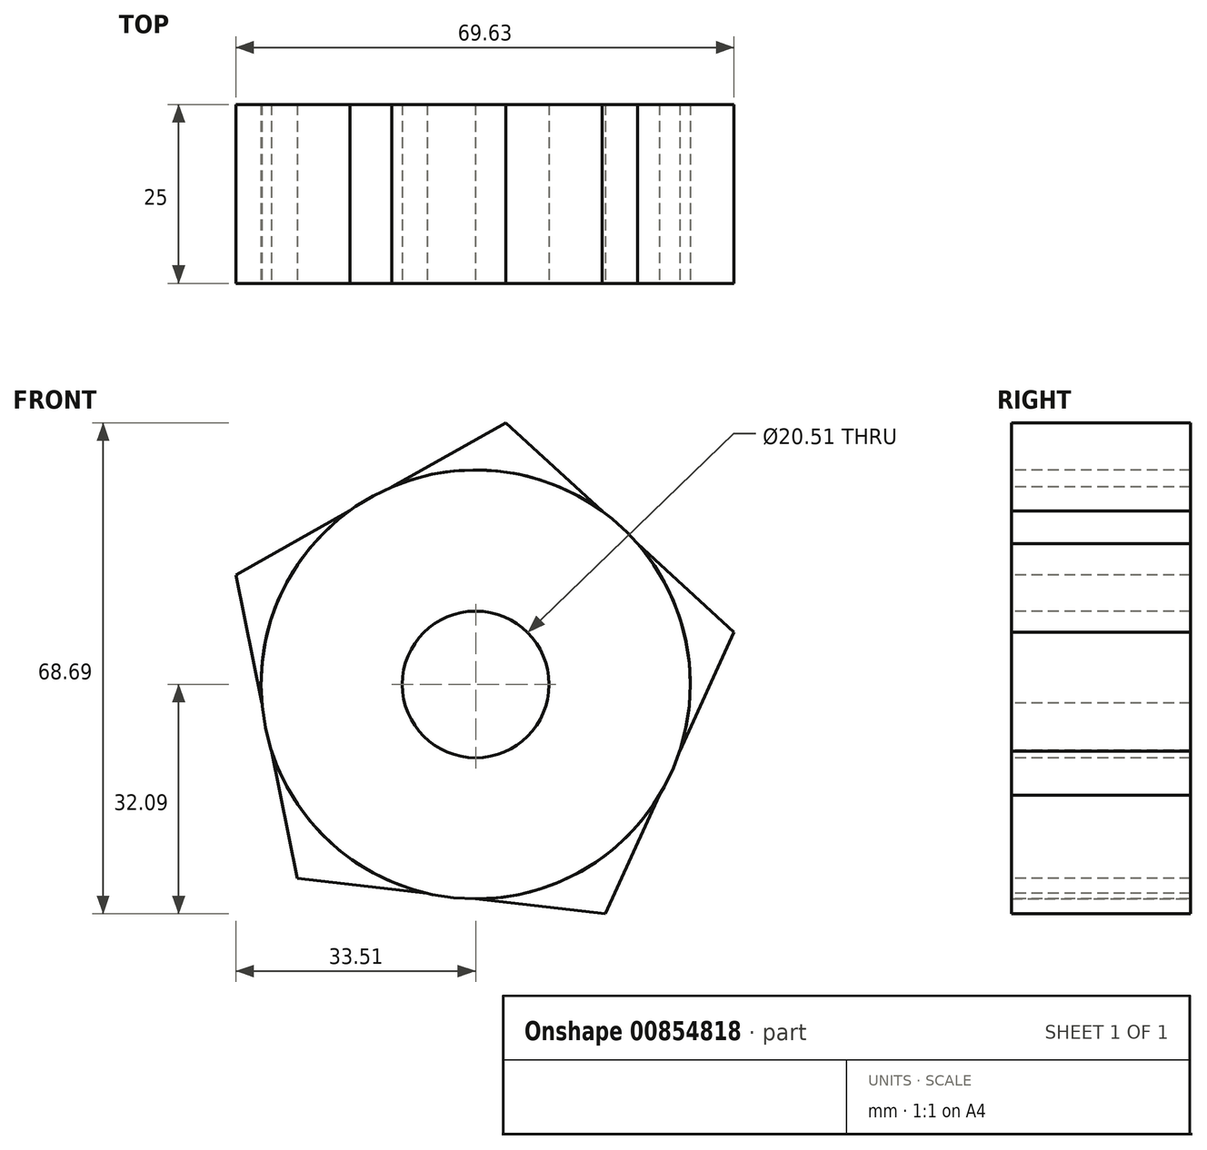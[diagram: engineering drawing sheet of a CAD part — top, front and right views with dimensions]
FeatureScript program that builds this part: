
annotation { "Feature Type Name" : "Feature", "Feature Type Description" : "" }
export const myFeature = defineFeature(function(context is Context, id is Id, definition is map)
    precondition{}
    {
        {
            var Q0;
            Q0=qCreatedBy(makeId("Front.planeOp"),FACE);
            var sketch = newSketch(context, id + "F0", { "sketchPlane" : qUnion([Q0])});
            skCircle(sketch, "E0", {"center": v(0, 0) * mm, "radius": 30 * mm});
            skSolve(sketch);
        }
        {
            var Q0;
            Q0=makeQuery(id+"F0.imprint","IMPRINT",FACE,{"disambiguationData":[TD([[makeQuery(id+"F0.imprint","IMPRINT",EDGE,{"derivedFrom":sQuery(id+"F0.wireOp",EDGE,"E0")}),1.0]])]});
            extrude(context, id + "F1", {"entities" : qUnion([Q0]), "depth" : 25 * mm, "offsetDistance" : 25 * mm});
        }
        {
            var Q0;
            Q0=makeQuery(id+"F1.opExtrude","CAP_FACE",FACE,{"disambiguationData":[OSD([sQuery(id+"F0.wireOp",EDGE,"E0")])],"isStart":false});
            var sketch = newSketch(context, id + "F2", { "sketchPlane" : qUnion([Q0])});
            skCircle(sketch, "E1", {"center": v(0, 0) * mm, "radius": 10.25 * mm});
            skSolve(sketch);
        }
        {
            var Q0;
            Q0=makeQuery(id+"F2.imprint","IMPRINT",FACE,{"disambiguationData":[TD([[makeQuery(id+"F2.imprint","IMPRINT",EDGE,{"derivedFrom":sQuery(id+"F2.wireOp",EDGE,"E1")}),1.0]])]});
            extrude(context, id + "F3", {"entities" : qUnion([Q0]), "operationType" : NewBodyOperationType.REMOVE, "endBound" : BoundingType.THROUGH_ALL, "oppositeDirection" : true, "depth" : 25 * mm, "offsetDistance" : 25 * mm});
        }
        {
            var Q0;
            Q0=makeQuery(id+"F2.imprint","IMPRINT",FACE,{"disambiguationData":[TD([[makeQuery(id+"F2.imprint","IMPRINT",EDGE,{"derivedFrom":sQuery(id+"F2.wireOp",EDGE,"E1")}),-1.0]])]});
            var sketch = newSketch(context, id + "F4", { "sketchPlane" : qUnion([Q0])});
            skCircle(sketch, "E2.cCircle", {"center": v(0, 0) * mm, "radius": 29.8 * mm, "construction": true});
            skLineSegment(sketch, "E2.0", {"start": v(-24.93, -27.13) * mm, "end": v(-33.5, 15.32) * mm});
            skLineSegment(sketch, "E2.1", {"start": v(-33.5, 15.32) * mm, "end": v(4.22, 36.6) * mm});
            skLineSegment(sketch, "E2.2", {"start": v(4.22, 36.6) * mm, "end": v(36.12, 7.3) * mm});
            skLineSegment(sketch, "E2.3", {"start": v(36.12, 7.3) * mm, "end": v(18.1, -32.1) * mm});
            skLineSegment(sketch, "E2.4", {"start": v(18.1, -32.1) * mm, "end": v(-24.93, -27.13) * mm});
            skPoint(sketch, "E2.0.midPoint", {"position": v(-29.22, -5.9) * mm});
            skSolve(sketch);
        }
        {
            var Q0;
            {var subQ0=sQuery(id+"F4.wireOp",EDGE,"E2.1");var subQ1=sQuery(id+"F4.wireOp",EDGE,"E2.0");var subQ2=makeQuery(id+"F4.imprint","INTERSECT",VERTEX,{"derivedFrom":[subQ1,subQ0]});Q0=makeQuery(id+"F4.imprint","IMPRINT",FACE,{"disambiguationData":[TD([[makeQuery(id+"F4.imprint","IMPRINT",EDGE,{"disambiguationData":[TD([[subQ2,1.0]])],"derivedFrom":subQ1}),-1.0]])]});}
            var Q1;
            {var subQ0=sQuery(id+"F4.wireOp",EDGE,"E2.2");var subQ1=sQuery(id+"F4.wireOp",EDGE,"E2.1");var subQ2=makeQuery(id+"F4.imprint","INTERSECT",VERTEX,{"derivedFrom":[subQ1,subQ0]});Q1=makeQuery(id+"F4.imprint","IMPRINT",FACE,{"disambiguationData":[TD([[makeQuery(id+"F4.imprint","IMPRINT",EDGE,{"disambiguationData":[TD([[subQ2,1.0]])],"derivedFrom":subQ1}),-1.0]])]});}
            var Q2;
            {var subQ0=sQuery(id+"F4.wireOp",EDGE,"E2.3");var subQ1=sQuery(id+"F4.wireOp",EDGE,"E2.2");var subQ2=makeQuery(id+"F4.imprint","INTERSECT",VERTEX,{"derivedFrom":[subQ1,subQ0]});Q2=makeQuery(id+"F4.imprint","IMPRINT",FACE,{"disambiguationData":[TD([[makeQuery(id+"F4.imprint","IMPRINT",EDGE,{"disambiguationData":[TD([[subQ2,1.0]])],"derivedFrom":subQ1}),-1.0]])]});}
            var Q3;
            {var subQ0=sQuery(id+"F4.wireOp",EDGE,"E2.4");var subQ1=sQuery(id+"F4.wireOp",EDGE,"E2.3");var subQ2=makeQuery(id+"F4.imprint","INTERSECT",VERTEX,{"derivedFrom":[subQ1,subQ0]});Q3=makeQuery(id+"F4.imprint","IMPRINT",FACE,{"disambiguationData":[TD([[makeQuery(id+"F4.imprint","IMPRINT",EDGE,{"disambiguationData":[TD([[subQ2,1.0]])],"derivedFrom":subQ1}),-1.0]])]});}
            var Q4;
            {var subQ0=sQuery(id+"F4.wireOp",EDGE,"E2.4");var subQ1=sQuery(id+"F4.wireOp",EDGE,"E2.0");var subQ2=makeQuery(id+"F4.imprint","INTERSECT",VERTEX,{"derivedFrom":[subQ1,subQ0]});Q4=makeQuery(id+"F4.imprint","IMPRINT",FACE,{"disambiguationData":[TD([[makeQuery(id+"F4.imprint","IMPRINT",EDGE,{"disambiguationData":[TD([[subQ2,-1.0]])],"derivedFrom":subQ1}),-1.0]])]});}
            extrude(context, id + "F5", {"entities" : qUnion([Q0, Q1, Q2, Q3, Q4]), "oppositeDirection" : true, "depth" : 25 * mm, "offsetDistance" : 25 * mm});
        }
    });
